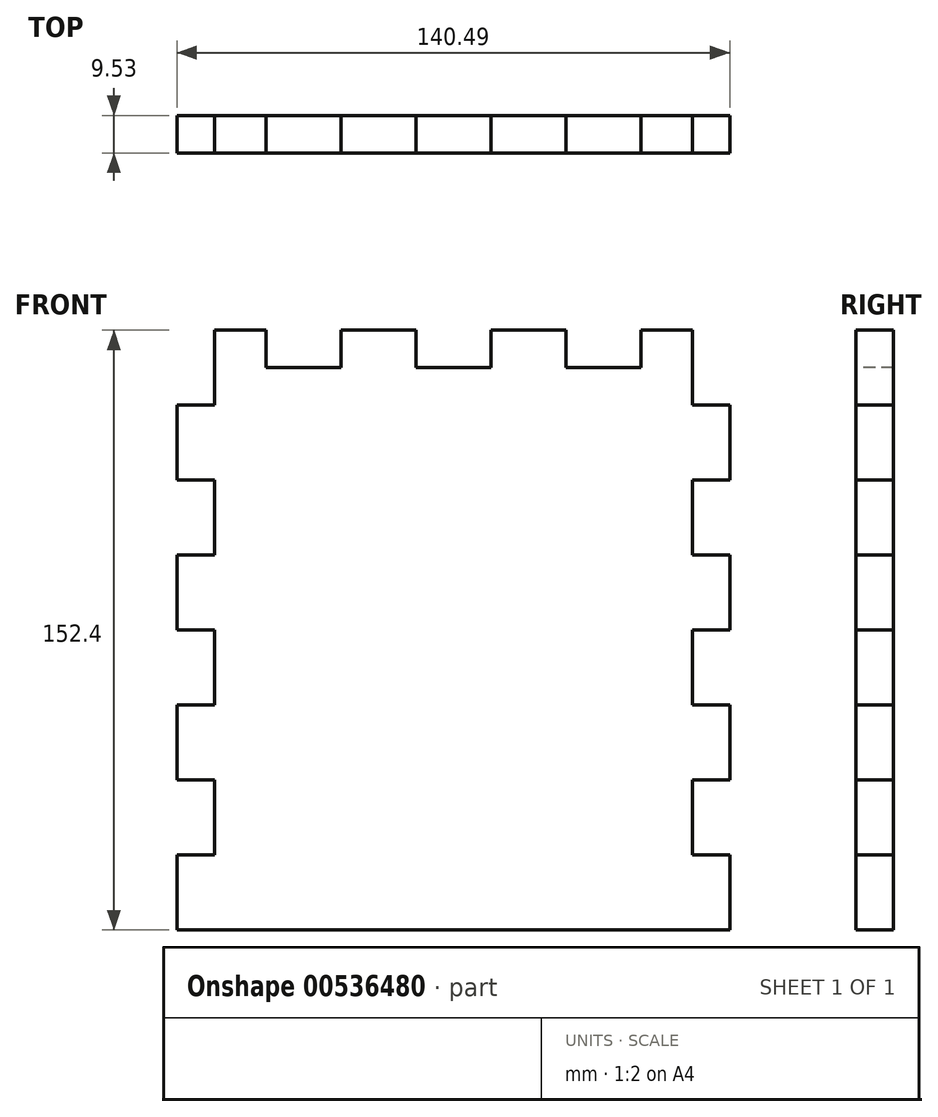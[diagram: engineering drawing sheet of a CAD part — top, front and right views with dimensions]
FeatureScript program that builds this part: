
annotation { "Feature Type Name" : "Feature", "Feature Type Description" : "" }
export const myFeature = defineFeature(function(context is Context, id is Id, definition is map)
    precondition{}
    {
        {
            var Q0;
            Q0=qCreatedBy(makeId("Front.planeOp"),FACE);
            var sketch = newSketch(context, id + "F0", { "sketchPlane" : qUnion([Q0])});
            skLineSegment(sketch, "E0", {"start": v(0, 0) * mm, "end": v(140.5, 0) * mm});
            skLineSegment(sketch, "E1", {"start": v(140.5, 0) * mm, "end": v(140.5, 152.4) * mm});
            skLineSegment(sketch, "E2", {"start": v(140.5, 152.4) * mm, "end": v(0, 152.4) * mm});
            skLineSegment(sketch, "E3", {"start": v(0, 152.4) * mm, "end": v(0, 0) * mm});
            skSolve(sketch);
        }
        {
            var Q0;
            Q0 = qSketchRegion(id + "F0", true);
            extrude(context, id + "F1", {"entities" : qUnion([Q0]), "depth" : 9.52 * mm, "offsetDistance" : 25.4 * mm});
        }
        {
            var Q0;
            Q0=makeQuery(id+"F1.opExtrude","CAP_FACE",FACE,{"disambiguationData":[OSD([sQuery(id+"F0.wireOp",EDGE,"E0"),sQuery(id+"F0.wireOp",EDGE,"E1"),sQuery(id+"F0.wireOp",EDGE,"E2"),sQuery(id+"F0.wireOp",EDGE,"E3")])],"isStart":false});
            var sketch = newSketch(context, id + "F2", { "sketchPlane" : qUnion([Q0])});
            skLineSegment(sketch, "E4", {"start": v(140.5, 0) * mm, "end": v(140.5, 19.05) * mm});
            skLineSegment(sketch, "E5", {"start": v(140.5, 19.05) * mm, "end": v(130.97, 19.05) * mm});
            skLineSegment(sketch, "E6", {"start": v(130.97, 19.05) * mm, "end": v(130.97, 38.1) * mm});
            skLineSegment(sketch, "E7", {"start": v(130.97, 38.1) * mm, "end": v(140.5, 38.1) * mm});
            skLineSegment(sketch, "E8.0.1.0", {"start": v(130.97, 57.15) * mm, "end": v(130.97, 76.2) * mm});
            skLineSegment(sketch, "E8.0.1.1", {"start": v(140.5, 57.15) * mm, "end": v(130.97, 57.15) * mm});
            skLineSegment(sketch, "E8.0.1.2", {"start": v(140.5, 38.1) * mm, "end": v(140.5, 57.15) * mm});
            skLineSegment(sketch, "E8.0.1.3", {"start": v(130.97, 76.2) * mm, "end": v(140.5, 76.2) * mm});
            skLineSegment(sketch, "E8.0.2.0", {"start": v(130.97, 95.25) * mm, "end": v(130.97, 114.3) * mm});
            skLineSegment(sketch, "E8.0.2.1", {"start": v(140.5, 95.25) * mm, "end": v(130.97, 95.25) * mm});
            skLineSegment(sketch, "E8.0.2.2", {"start": v(140.5, 76.2) * mm, "end": v(140.5, 95.25) * mm});
            skLineSegment(sketch, "E8.0.2.3", {"start": v(130.97, 114.3) * mm, "end": v(140.5, 114.3) * mm});
            skLineSegment(sketch, "E8.0.3.0", {"start": v(130.97, 133.35) * mm, "end": v(130.97, 152.4) * mm});
            skLineSegment(sketch, "E8.0.3.1", {"start": v(140.5, 133.35) * mm, "end": v(130.97, 133.35) * mm});
            skLineSegment(sketch, "E8.0.3.2", {"start": v(140.5, 114.3) * mm, "end": v(140.5, 133.35) * mm});
            skLineSegment(sketch, "E8.0.3.3", {"start": v(130.97, 152.4) * mm, "end": v(140.5, 152.4) * mm, "construction": true});
            skLineSegment(sketch, "E8.direction1", {"start": v(140.5, 0) * mm, "end": v(165.9, 0) * mm, "construction": true});
            skLineSegment(sketch, "E8.direction2", {"start": v(140.5, 0) * mm, "end": v(140.5, 38.1) * mm, "construction": true});
            skLineSegment(sketch, "E9", {"start": v(70.25, 0) * mm, "end": v(70.25, 152.4) * mm, "construction": true});
            skLineSegment(sketch, "E10.MirrorCS", {"start": v(9.52, 114.3) * mm, "end": v(0, 114.3) * mm});
            skLineSegment(sketch, "E11.MirrorCS", {"start": v(0, 95.25) * mm, "end": v(9.52, 95.25) * mm});
            skLineSegment(sketch, "E12.MirrorCS", {"start": v(9.52, 76.2) * mm, "end": v(0, 76.2) * mm});
            skLineSegment(sketch, "E13.MirrorCS", {"start": v(0, 57.15) * mm, "end": v(9.52, 57.15) * mm});
            skLineSegment(sketch, "E14.MirrorCS", {"start": v(9.53, 38.1) * mm, "end": v(0, 38.1) * mm});
            skLineSegment(sketch, "E15.MirrorCS", {"start": v(0, 19.05) * mm, "end": v(9.53, 19.05) * mm});
            skLineSegment(sketch, "E16.MirrorCS", {"start": v(9.52, 152.4) * mm, "end": v(0, 152.4) * mm, "construction": true});
            skLineSegment(sketch, "E17.MirrorCS", {"start": v(0, 114.3) * mm, "end": v(0, 133.35) * mm});
            skLineSegment(sketch, "E18.MirrorCS", {"start": v(0, 133.35) * mm, "end": v(9.52, 133.35) * mm});
            skLineSegment(sketch, "E19.MirrorCS", {"start": v(9.52, 133.35) * mm, "end": v(9.52, 152.4) * mm});
            skLineSegment(sketch, "E20.MirrorCS", {"start": v(0, 76.2) * mm, "end": v(0, 95.25) * mm});
            skLineSegment(sketch, "E21.MirrorCS", {"start": v(9.52, 95.25) * mm, "end": v(9.52, 114.3) * mm});
            skLineSegment(sketch, "E22.MirrorCS", {"start": v(9.52, 57.15) * mm, "end": v(9.52, 76.2) * mm});
            skLineSegment(sketch, "E23.MirrorCS", {"start": v(9.53, 19.05) * mm, "end": v(9.52, 38.1) * mm});
            skLineSegment(sketch, "E24.MirrorCS", {"start": v(0, 0) * mm, "end": v(0, 19.05) * mm, "construction": true});
            skLineSegment(sketch, "E25.MirrorCS", {"start": v(0, 38.1) * mm, "end": v(0, 57.15) * mm});
            skLineSegment(sketch, "E26.MirrorCS", {"start": v(0, 0) * mm, "end": v(0, 38.1) * mm, "construction": true});
            skLineSegment(sketch, "E27", {"start": v(22.62, 142.87) * mm, "end": v(41.67, 142.87) * mm});
            skLineSegment(sketch, "E28", {"start": v(41.67, 142.87) * mm, "end": v(41.67, 152.4) * mm});
            skLineSegment(sketch, "E29", {"start": v(41.67, 152.4) * mm, "end": v(60.72, 152.4) * mm});
            skLineSegment(sketch, "E30", {"start": v(60.72, 152.4) * mm, "end": v(60.72, 142.87) * mm});
            skLineSegment(sketch, "E31", {"start": v(60.72, 142.87) * mm, "end": v(79.77, 142.87) * mm});
            skLineSegment(sketch, "E32", {"start": v(79.77, 142.87) * mm, "end": v(79.77, 152.4) * mm});
            skLineSegment(sketch, "E33", {"start": v(79.77, 152.4) * mm, "end": v(98.82, 152.4) * mm});
            skLineSegment(sketch, "E34", {"start": v(98.82, 152.4) * mm, "end": v(98.82, 142.87) * mm});
            skLineSegment(sketch, "E35", {"start": v(98.82, 142.87) * mm, "end": v(117.87, 142.87) * mm});
            skLineSegment(sketch, "E36", {"start": v(117.87, 142.87) * mm, "end": v(117.87, 152.4) * mm});
            skLineSegment(sketch, "E37", {"start": v(117.87, 152.4) * mm, "end": v(130.97, 152.4) * mm});
            skPoint(sketch, "E38", {"position": v(70.25, 142.87) * mm});
            skLineSegment(sketch, "E39", {"start": v(22.62, 142.87) * mm, "end": v(22.62, 152.4) * mm});
            skLineSegment(sketch, "E40", {"start": v(22.62, 152.4) * mm, "end": v(9.52, 152.4) * mm});
            skLineSegment(sketch, "E41", {"start": v(0, 19.05) * mm, "end": v(0, 0) * mm});
            skSolve(sketch);
        }
        {
            var Q0;
            Q0 = qSketchRegion(id + "F2", true);
            var Q1;
            {var subQ0=sQuery(id+"F2.wireOp",EDGE,"E18.MirrorCS");Q1=makeQuery(id+"F2.imprint","IMPRINT",FACE,{"disambiguationData":[TD([[makeQuery(id+"F2.imprint","IMPRINT",EDGE,{"derivedFrom":subQ0}),1.0]])]});}
            var Q2;
            {var subQ0=sQuery(id+"F2.wireOp",EDGE,"E10.MirrorCS");Q2=makeQuery(id+"F2.imprint","IMPRINT",FACE,{"disambiguationData":[TD([[makeQuery(id+"F2.imprint","IMPRINT",EDGE,{"derivedFrom":subQ0}),1.0]])]});}
            var Q3;
            {var subQ0=sQuery(id+"F2.wireOp",EDGE,"E12.MirrorCS");Q3=makeQuery(id+"F2.imprint","IMPRINT",FACE,{"disambiguationData":[TD([[makeQuery(id+"F2.imprint","IMPRINT",EDGE,{"derivedFrom":subQ0}),1.0]])]});}
            var Q4;
            {var subQ0=sQuery(id+"F2.wireOp",EDGE,"E14.MirrorCS");Q4=makeQuery(id+"F2.imprint","IMPRINT",FACE,{"disambiguationData":[TD([[makeQuery(id+"F2.imprint","IMPRINT",EDGE,{"derivedFrom":subQ0}),1.0]])]});}
            var Q5;
            Q5=makeQuery(id+"F2.imprint","IMPRINT",FACE,{"disambiguationData":[TD([[makeQuery(id+"F2.imprint","IMPRINT",EDGE,{"derivedFrom":sQuery(id+"F2.wireOp",EDGE,"E27")}),1.0]])]});
            var Q6;
            {var subQ0=sQuery(id+"F2.wireOp",EDGE,"E30");Q6=makeQuery(id+"F2.imprint","IMPRINT",FACE,{"disambiguationData":[TD([[makeQuery(id+"F2.imprint","IMPRINT",EDGE,{"derivedFrom":subQ0}),1.0]])]});}
            var Q7;
            {var subQ0=sQuery(id+"F2.wireOp",EDGE,"E34");Q7=makeQuery(id+"F2.imprint","IMPRINT",FACE,{"disambiguationData":[TD([[makeQuery(id+"F2.imprint","IMPRINT",EDGE,{"derivedFrom":subQ0}),1.0]])]});}
            var Q8;
            {var subQ0=sQuery(id+"F2.wireOp",EDGE,"E8.0.3.0");Q8=makeQuery(id+"F2.imprint","IMPRINT",FACE,{"disambiguationData":[TD([[makeQuery(id+"F2.imprint","IMPRINT",EDGE,{"derivedFrom":subQ0}),-1.0]])]});}
            var Q9;
            Q9=makeQuery(id+"F2.imprint","IMPRINT",FACE,{"disambiguationData":[TD([[makeQuery(id+"F2.imprint","IMPRINT",EDGE,{"derivedFrom":sQuery(id+"F2.wireOp",EDGE,"E8.0.2.0")}),-1.0]])]});
            var Q10;
            Q10=makeQuery(id+"F2.imprint","IMPRINT",FACE,{"disambiguationData":[TD([[makeQuery(id+"F2.imprint","IMPRINT",EDGE,{"derivedFrom":sQuery(id+"F2.wireOp",EDGE,"E8.0.1.0")}),-1.0]])]});
            var Q11;
            {var subQ0=sQuery(id+"F2.wireOp",EDGE,"E5");Q11=makeQuery(id+"F2.imprint","IMPRINT",FACE,{"disambiguationData":[TD([[makeQuery(id+"F2.imprint","IMPRINT",EDGE,{"derivedFrom":subQ0}),-1.0]])]});}
            extrude(context, id + "F3", {"entities" : qUnion([Q0, Q1, Q2, Q3, Q4, Q5, Q6, Q7, Q8, Q9, Q10, Q11]), "operationType" : NewBodyOperationType.REMOVE, "oppositeDirection" : true, "depth" : 25.4 * mm, "offsetDistance" : 25.4 * mm});
        }
    });
